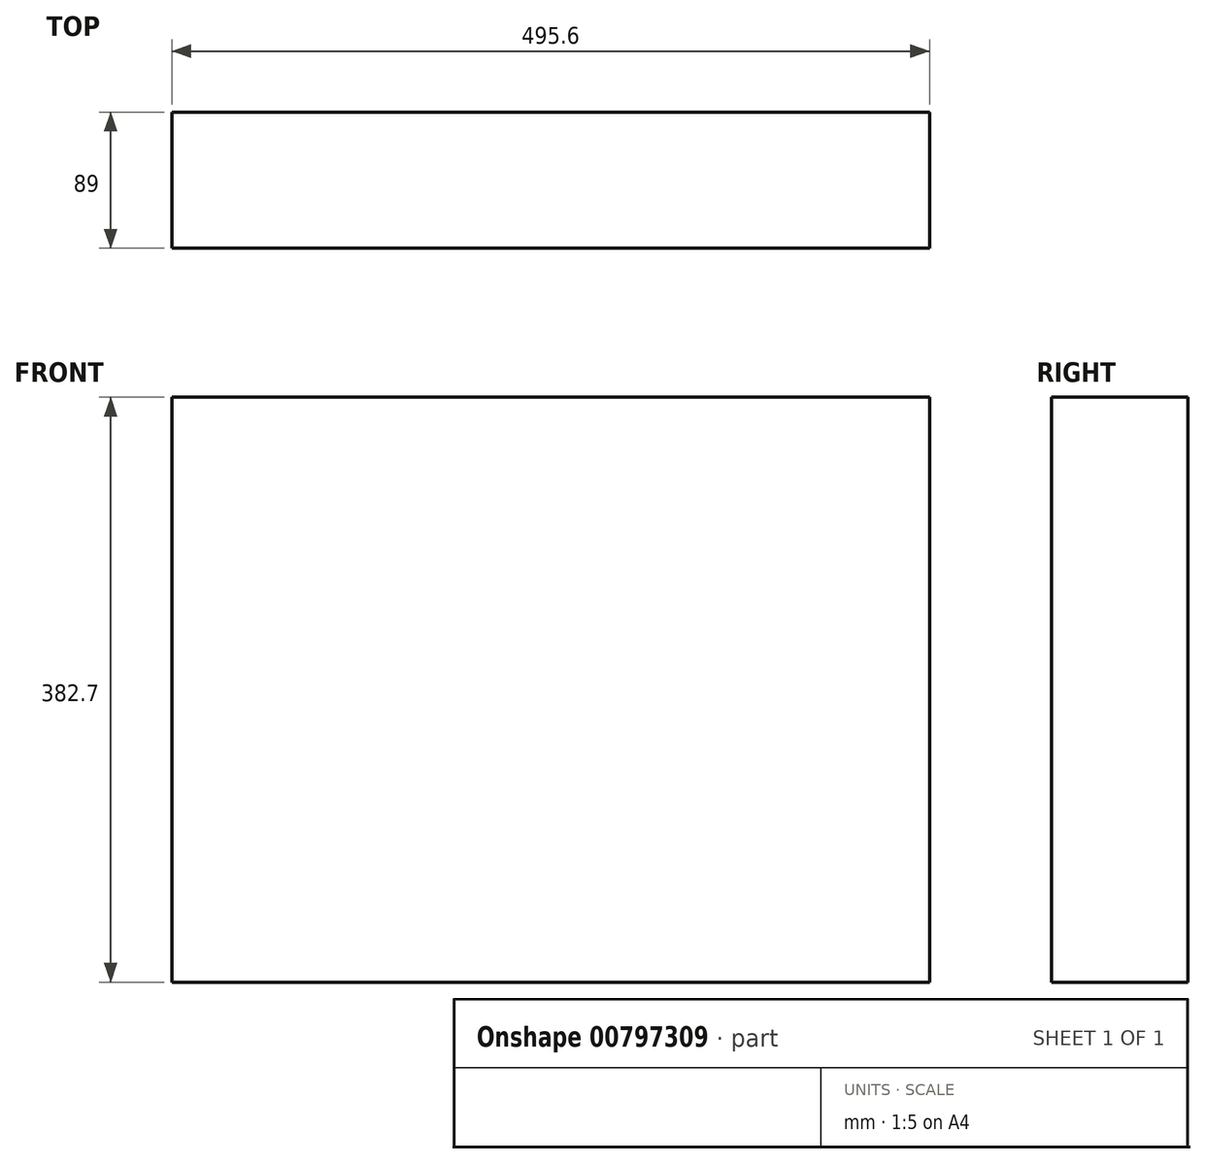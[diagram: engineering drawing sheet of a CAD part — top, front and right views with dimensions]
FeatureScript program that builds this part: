
annotation { "Feature Type Name" : "Feature", "Feature Type Description" : "" }
export const myFeature = defineFeature(function(context is Context, id is Id, definition is map)
    precondition{}
    {
        {
            var Q0;
            Q0=qCreatedBy(makeId("Front.planeOp"),FACE);
            var sketch = newSketch(context, id + "F0", { "sketchPlane" : qUnion([Q0])});
            skLineSegment(sketch, "E0.bottom", {"start": v(247.8, 191.35) * mm, "end": v(-247.8, 191.35) * mm});
            skLineSegment(sketch, "E0.top", {"start": v(247.8, -191.35) * mm, "end": v(-247.8, -191.35) * mm});
            skLineSegment(sketch, "E0.left", {"start": v(247.8, 191.35) * mm, "end": v(247.8, -191.35) * mm});
            skLineSegment(sketch, "E0.right", {"start": v(-247.8, 191.35) * mm, "end": v(-247.8, -191.35) * mm});
            skPoint(sketch, "E0.middle", {"position": v(0, 0) * mm});
            skSolve(sketch);
        }
        {
            var Q0;
            Q0=qSketchRegion(id+"F0",true);
            extrude(context, id + "F1", {"entities" : qUnion([Q0]), "depth" : 89 * mm, "offsetDistance" : 25 * mm, "symmetric" : true});
        }
    });
